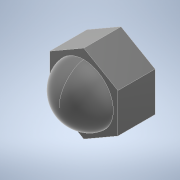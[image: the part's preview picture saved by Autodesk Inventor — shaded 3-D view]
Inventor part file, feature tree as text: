
AUTODESK INVENTOR PART (.ipt)
format: ipt  version: 2022 (Build 260153000, 153)  size: 175,616 bytes
history: native  units: mm
features: sketch x2, extrude x1, revolve x1, thread x1
ambient origin geometry x8: Origin, YZ Plane, XZ Plane, XY Plane, X Axis, Y Axis, Z Axis, Center Point
bodies: Solid1 (feature_tree)
feature tree (5):
  extrude  "Extrusion1"  Depth=3.0mm
  revolve  "Revolution1"  [1 undecoded]
  thread  "Thread1"  [1 undecoded]
  sketch  "Sketch1"  dims[d0=5.5mm d1=3.0mm]
  sketch  "Sketch2"  dims[d2=3.0mm d3=0.0mm d4=5.0mm d5=90.0deg d6=3.0mm d7=0.0mm]
note: 2 required parameter values undecoded (feature->parameter linkage not recoverable at this tier; creation-order binding heuristic only, values carry confidence <= 0.55)